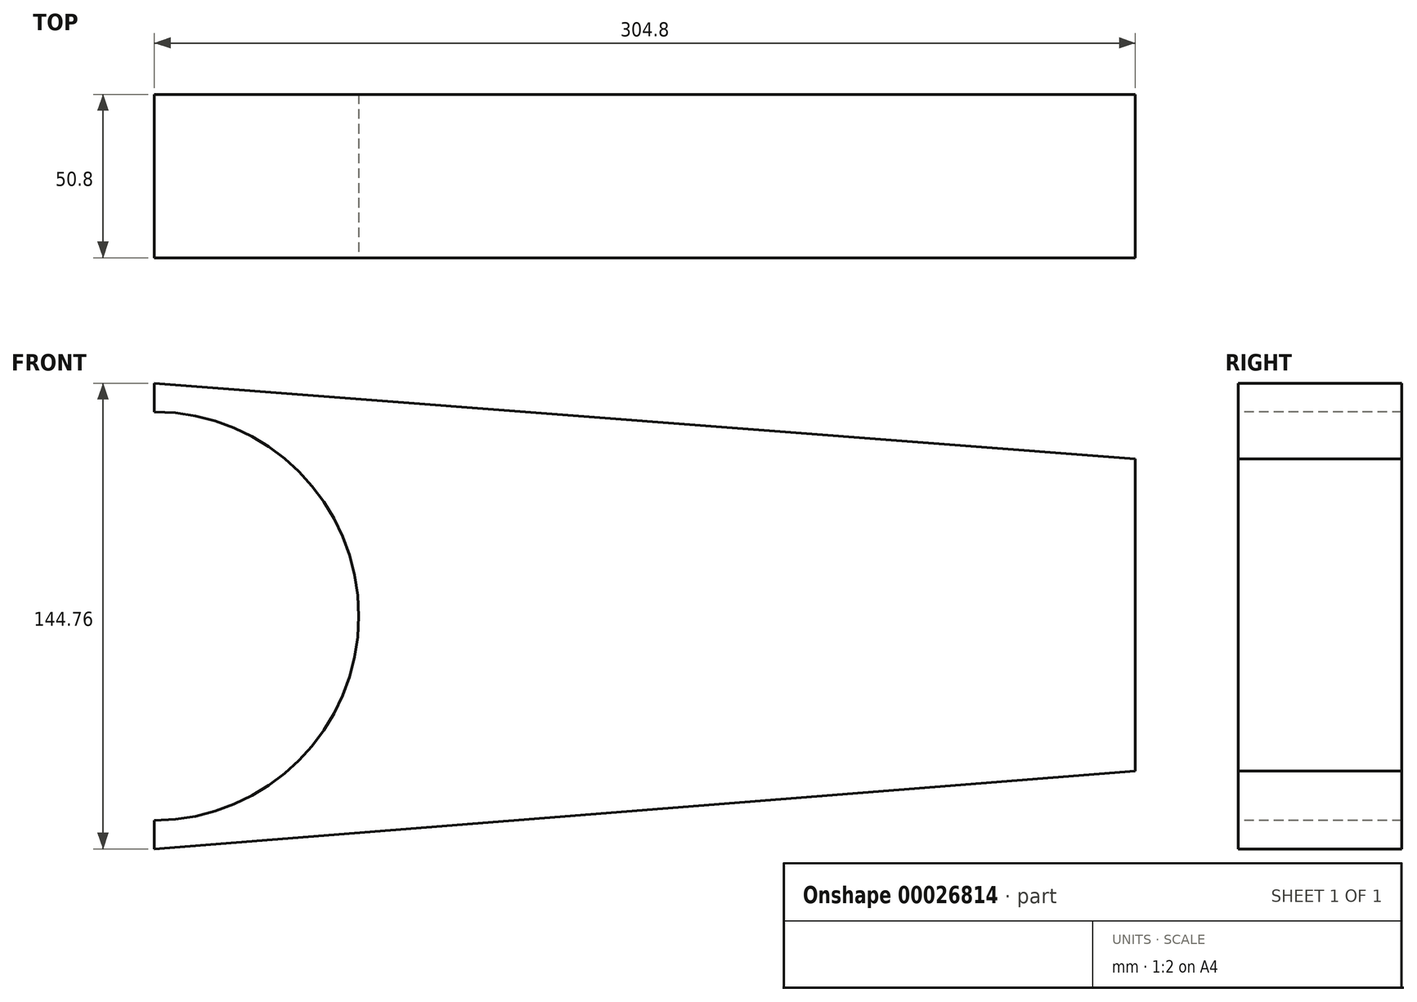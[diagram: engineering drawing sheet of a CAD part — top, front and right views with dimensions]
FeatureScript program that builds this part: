
annotation { "Feature Type Name" : "Feature", "Feature Type Description" : "" }
export const myFeature = defineFeature(function(context is Context, id is Id, definition is map)
    precondition{}
    {
        {
            var Q0;
            Q0=qCreatedBy(makeId("Front.planeOp"),FACE);
            var sketch = newSketch(context, id + "F0", { "sketchPlane" : qUnion([Q0])});
            skLineSegment(sketch, "E0.left", {"start": v(-130.2, 119.57) * mm, "end": v(-130.2, -25.2) * mm});
            skLineSegment(sketch, "E0.right", {"start": v(174.6, 95.98) * mm, "end": v(174.6, -0.98) * mm});
            skLineSegment(sketch, "E1", {"start": v(-130.2, 119.57) * mm, "end": v(174.6, 95.98) * mm});
            skLineSegment(sketch, "E2", {"start": v(-130.2, -25.2) * mm, "end": v(174.6, -0.98) * mm});
            skPoint(sketch, "E3.orphan", {"position": v(174.6, 124.47) * mm});
            skPoint(sketch, "E0.top.end.orphan", {"position": v(174.6, -27.93) * mm});
            skSolve(sketch);
        }
        {
            var Q0;
            Q0 = qSketchRegion(id + "F0", true);
            extrude(context, id + "F1", {"entities" : qUnion([Q0]), "depth" : 50.8 * mm});
        }
        {
            var Q0;
            Q0=makeQuery(id+"F1.opExtrude","CAP_FACE",FACE,{"disambiguationData":[OSD([sQuery(id+"F0.wireOp",EDGE,"E0.bottom"),sQuery(id+"F0.wireOp",EDGE,"E0.top"),sQuery(id+"F0.wireOp",EDGE,"E0.left"),sQuery(id+"F0.wireOp",EDGE,"E0.right")])],"isStart":false});
            var sketch = newSketch(context, id + "F2", { "sketchPlane" : qUnion([Q0])});
            skArc(sketch, "E4", {"start": v(-130.2, -16.31) * mm, "mid": v(-66.7, 47.19) * mm, "end": v(-130.2, 110.69) * mm});
            skLineSegment(sketch, "E5", {"start": v(-130.2, -16.31) * mm, "end": v(-130.2, 110.69) * mm});
            skSolve(sketch);
        }
        {
            var Q0;
            Q0=makeQuery(id+"F2.imprint","IMPRINT",FACE,{"disambiguationData":[TD([[makeQuery(id+"F2.imprint","IMPRINT",EDGE,{"derivedFrom":sQuery(id+"F2.wireOp",EDGE,"E4")}),1.0]])]});
            extrude(context, id + "F3", {"entities" : qUnion([Q0]), "operationType" : NewBodyOperationType.REMOVE, "oppositeDirection" : true, "depth" : 50.8 * mm});
        }
    });
